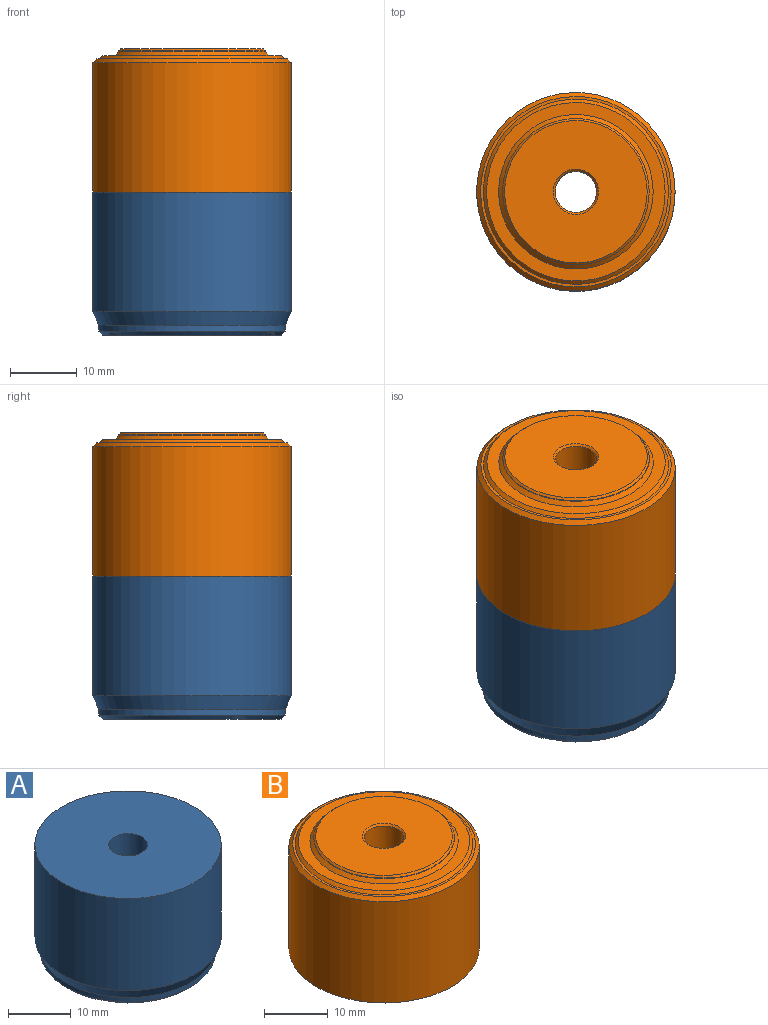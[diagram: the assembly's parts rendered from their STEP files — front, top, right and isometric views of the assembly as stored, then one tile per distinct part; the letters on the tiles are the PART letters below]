
ASSEMBLY  parts=2 mates=1
PART A: 44 faces, bbox 29.8x29.8x21.5 mm
  f0: cylinder r=14mm len=28mm, axis (0,0,1), area 79.2mm2, adj f17,f39
  f1: cylinder r=3.1mm len=20.9mm, axis (0,0,-1), area 407.1mm2, adj f3,f30
  f2: cylinder r=14.9mm len=29.8mm, axis (0,0,-1), area 1685.2mm2, adj f3,f17
  f3: plane 29.8x29.8mm, normal (0,0,1), area 667.3mm2, adj f1,f2
  f4: cylinder r=1.5mm len=3mm, axis (0,0,1), area 6.6mm2, adj f5,f15,f29,f32
  f5: plane 3x1.4mm, normal (1,0,0), area 4.2mm2, adj f4,f6,f28,f35
  f6: cylinder r=1.5mm len=3mm, axis (0,0,1), area 6.6mm2, adj f5,f15,f26,f38
  f7: plane 2.6x1.5mm, normal (-0.5,0.87,0), area 4.2mm2, adj f8,f13,f19,f33
  f8: cylinder r=1.5mm len=2.8mm, axis (0,0,1), area 6.6mm2, adj f7,f9,f21,f37
  f9: plane 2.6x1.5mm, normal (0.5,-0.87,0), area 4.2mm2, adj f8,f13,f20,f34
  f10: plane 2.6x1.5mm, normal (-0.5,-0.87,0), area 4.2mm2, adj f11,f14,f23,f42
  f11: cylinder r=1.5mm len=2.8mm, axis (0,0,1), area 6.6mm2, adj f10,f12,f25,f40
  f12: plane 2.6x1.5mm, normal (0.5,0.87,0), area 4.2mm2, adj f11,f14,f24,f41
  f13: cylinder r=1.5mm len=2.8mm, axis (0,0,1), area 6.6mm2, adj f7,f9,f18,f31
  f14: cylinder r=1.5mm len=2.8mm, axis (0,0,1), area 6.6mm2, adj f10,f12,f22,f43
  f15: plane 3x1.4mm, normal (-1,0,0), area 4.2mm2, adj f4,f6,f27,f36
  f16: plane 26.8x26.68mm, normal (0,0,-1), area 448.7mm2, adj f30,f31,f32,f33,f34,f35,f36,f37
  f17: cone r=14.9mm half-angle=24.2deg, axis (0,0,1), area 199.1mm2, adj f0,f2
  f18: cone r=1.5mm half-angle=45deg, axis (0,0,-1), area 5mm2, adj f13,f19,f20
  f19: plane 3.35x2.8mm, normal (-0.35,0.61,-0.71), area 6.4mm2, adj f7,f18,f20,f21
  f20: plane 3.35x2.8mm, normal (0.35,-0.61,-0.71), area 6.4mm2, adj f9,f18,f19,f21
  f21: cone r=1.5mm half-angle=45deg, axis (0,0,-1), area 5mm2, adj f8,f19,f20
  f22: cone r=1.5mm half-angle=45deg, axis (0,0,-1), area 5mm2, adj f14,f23,f24
  f23: plane 3.35x2.8mm, normal (-0.35,-0.61,-0.71), area 6.4mm2, adj f10,f22,f24,f25
  f24: plane 3.35x2.8mm, normal (0.35,0.61,-0.71), area 6.4mm2, adj f12,f22,f23,f25
  f25: cone r=1.5mm half-angle=45deg, axis (0,0,-1), area 5mm2, adj f11,f23,f24
  f26: cone r=1.5mm half-angle=45deg, axis (0,0,-1), area 5mm2, adj f6,f27,f28
  f27: plane 3x1.5mm, normal (-0.71,0,-0.71), area 6.4mm2, adj f15,f26,f28,f29
  f28: plane 3x1.5mm, normal (0.71,0,-0.71), area 6.4mm2, adj f5,f26,f27,f29
  f29: cone r=1.5mm half-angle=45deg, axis (0,0,-1), area 5mm2, adj f4,f27,f28
  f30: cone r=3.7mm half-angle=45deg, axis (0,0,-1), area 18.1mm2, adj f1,f16
  f31: cone r=1.5mm half-angle=45deg, axis (0,0,-1), area 4.8mm2, adj f13,f16,f33,f34
  f32: cone r=1.5mm half-angle=45deg, axis (0,0,-1), area 4.8mm2, adj f4,f16,f35,f36
  f33: plane 2.9x2.02mm, normal (-0.35,0.61,-0.71), area 2.5mm2, adj f7,f16,f31,f37
  f34: plane 2.9x2.02mm, normal (0.35,-0.61,-0.71), area 2.5mm2, adj f9,f16,f31,f37
  f35: plane 3x0.6mm, normal (0.71,0,-0.71), area 2.5mm2, adj f5,f16,f32,f38
  f36: plane 3x0.6mm, normal (-0.71,0,-0.71), area 2.5mm2, adj f15,f16,f32,f38
  f37: cone r=1.5mm half-angle=45deg, axis (0,0,-1), area 3.1mm2, adj f8,f16,f33,f34,f39
  f38: cone r=1.5mm half-angle=45deg, axis (0,0,-1), area 3.1mm2, adj f6,f16,f35,f36,f39
  f39: cone r=14mm half-angle=45deg, axis (0,0,1), area 68.4mm2, adj f0,f16,f37,f38,f40
  f40: cone r=1.5mm half-angle=45deg, axis (0,0,-1), area 3.1mm2, adj f11,f16,f39,f41,f42
  f41: plane 2.9x2.02mm, normal (0.35,0.61,-0.71), area 2.5mm2, adj f12,f16,f40,f43
  f42: plane 2.9x2.02mm, normal (-0.35,-0.61,-0.71), area 2.5mm2, adj f10,f16,f40,f43
  f43: cone r=1.5mm half-angle=45deg, axis (0,0,-1), area 4.8mm2, adj f14,f16,f41,f42
PART B: 12 faces, bbox 29.8x29.8x21.5 mm
  f0: cylinder r=3.1mm len=21.2mm, axis (0,0,1), area 412.9mm2, adj f2,f11
  f1: cylinder r=14.9mm len=29.8mm, axis (0,0,1), area 1816.2mm2, adj f2,f9
  f2: plane 29.8x29.8mm, normal (0,0,-1), area 667.3mm2, adj f0,f1
  f3: plane 28.6x28.6mm, normal (0,0,1), area 35.4mm2, adj f8,f9
  f4: plane 26.8x26.8mm, normal (0,0,1), area 141.4mm2, adj f7,f8
  f5: cylinder r=11mm len=22mm, axis (0,0,-1), area 6.9mm2, adj f7,f10
  f6: plane 21.4x21.4mm, normal (0,0,1), area 323.4mm2, adj f10,f11
  f7: cone r=11mm half-angle=45deg, axis (0,0,-1), area 60.2mm2, adj f4,f5
  f8: cone r=13.4mm half-angle=45deg, axis (0,0,-1), area 60.6mm2, adj f3,f4
  f9: cone r=14.3mm half-angle=45deg, axis (0,0,-1), area 77.8mm2, adj f1,f3
  f10: cone r=10.7mm half-angle=45deg, axis (0,0,-1), area 28.9mm2, adj f5,f6
  f11: cone r=3.1mm half-angle=45deg, axis (0,0,1), area 8.7mm2, adj f0,f6
PLACE A t=(9.7,0.87,-14.22)mm
PLACE B t=(9.7,0.87,23.78)mm
MATE fastened B.f0 <-> A.f2  axis (0,0,-1) through (9.7,0.87,3.78)mm
